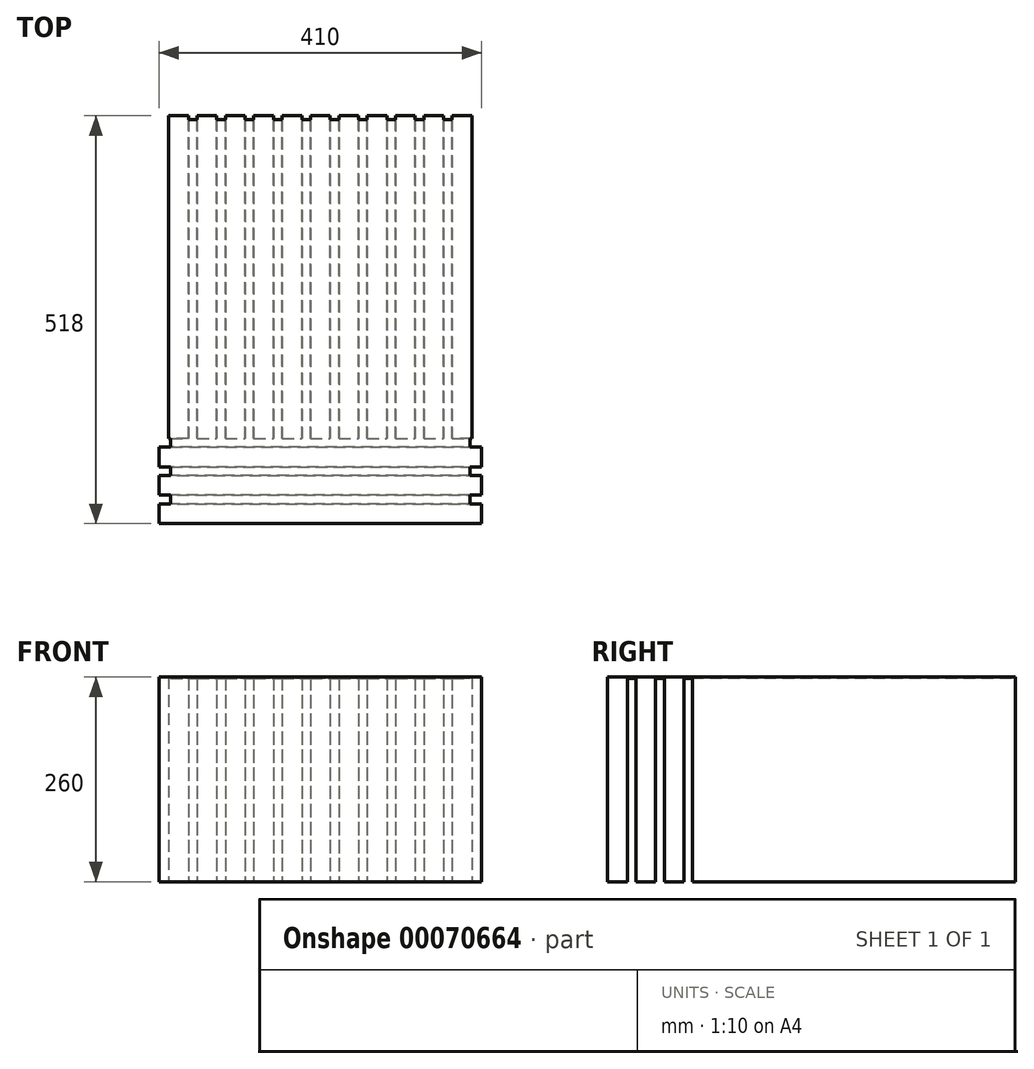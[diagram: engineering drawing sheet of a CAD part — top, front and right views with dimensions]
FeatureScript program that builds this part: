
annotation { "Feature Type Name" : "Feature", "Feature Type Description" : "" }
export const myFeature = defineFeature(function(context is Context, id is Id, definition is map)
    precondition{}
    {
        {
            var Q0;
            Q0=qCreatedBy(makeId("Top.planeOp"),FACE);
            cPlane(context, id + "F0", {"entities" : qUnion([Q0]), "cplaneType" : CPlaneType.OFFSET, "offset" : 258 * mm, "width" : 150 * mm, "height" : 150 * mm});
        }
        {
            var Q0;
            Q0=qCreatedBy(id+"F0.planeOp",FACE);
            var sketch = newSketch(context, id + "F1", { "sketchPlane" : qUnion([Q0])});
            skLineSegment(sketch, "E0.bottom", {"start": v(-190, 200) * mm, "end": v(190, 200) * mm});
            skLineSegment(sketch, "E0.top", {"start": v(-190, -300) * mm, "end": v(190, -300) * mm});
            skLineSegment(sketch, "E0.left", {"start": v(-190, 200) * mm, "end": v(-190, -300) * mm});
            skLineSegment(sketch, "E0.right", {"start": v(190, 200) * mm, "end": v(190, -300) * mm});
            skSolve(sketch);
        }
        {
            var Q0;
            Q0 = qSketchRegion(id + "F1", true);
            extrude(context, id + "F2", {"entities" : qUnion([Q0]), "depth" : 2 * mm});
        }
        {
            var Q0;
            Q0=qCreatedBy(makeId("Top.planeOp"),FACE);
            var sketch = newSketch(context, id + "F3", { "sketchPlane" : qUnion([Q0])});
            skLineSegment(sketch, "E1.rect.bottom", {"start": v(12.5, -205) * mm, "end": v(-12.5, -205) * mm});
            skLineSegment(sketch, "E1.rect.top", {"start": v(12.5, 205) * mm, "end": v(-12.5, 205) * mm});
            skLineSegment(sketch, "E1.rect.left", {"start": v(12.5, -205) * mm, "end": v(12.5, 205) * mm});
            skLineSegment(sketch, "E1.rect.right", {"start": v(-12.5, -205) * mm, "end": v(-12.5, 205) * mm});
            skPoint(sketch, "E1.rect.middle", {"position": v(0, 0) * mm});
            skLineSegment(sketch, "E2.1.0.0", {"start": v(48.5, -205) * mm, "end": v(23.5, -205) * mm});
            skLineSegment(sketch, "E2.1.0.1", {"start": v(48.5, -205) * mm, "end": v(48.5, 205) * mm});
            skLineSegment(sketch, "E2.1.0.2", {"start": v(23.5, -205) * mm, "end": v(23.5, 205) * mm});
            skPoint(sketch, "E2.1.0.3", {"position": v(36, 0) * mm});
            skLineSegment(sketch, "E2.1.0.4", {"start": v(48.5, 205) * mm, "end": v(23.5, 205) * mm});
            skLineSegment(sketch, "E2.2.0.0", {"start": v(84.5, -205) * mm, "end": v(59.5, -205) * mm});
            skLineSegment(sketch, "E2.2.0.1", {"start": v(84.5, -205) * mm, "end": v(84.5, 205) * mm});
            skLineSegment(sketch, "E2.2.0.2", {"start": v(59.5, -205) * mm, "end": v(59.5, 205) * mm});
            skPoint(sketch, "E2.2.0.3", {"position": v(72, 0) * mm});
            skLineSegment(sketch, "E2.2.0.4", {"start": v(84.5, 205) * mm, "end": v(59.5, 205) * mm});
            skLineSegment(sketch, "E2.direction1", {"start": v(-12.5, -205) * mm, "end": v(23.5, -205) * mm, "construction": true});
            skLineSegment(sketch, "E3.0.3.0", {"start": v(120.5, -205) * mm, "end": v(95.5, -205) * mm});
            skLineSegment(sketch, "E3.3.3.0", {"start": v(120.5, -205) * mm, "end": v(120.5, 205) * mm});
            skLineSegment(sketch, "E3.6.3.0", {"start": v(95.5, -205) * mm, "end": v(95.5, 205) * mm});
            skPoint(sketch, "E3.9.3.0", {"position": v(108, 0) * mm});
            skLineSegment(sketch, "E3.10.3.0", {"start": v(120.5, 205) * mm, "end": v(95.5, 205) * mm});
            skLineSegment(sketch, "E3.0.4.0", {"start": v(156.5, -205) * mm, "end": v(131.5, -205) * mm});
            skLineSegment(sketch, "E3.3.4.0", {"start": v(156.5, -205) * mm, "end": v(156.5, 205) * mm});
            skLineSegment(sketch, "E3.6.4.0", {"start": v(131.5, -205) * mm, "end": v(131.5, 205) * mm});
            skPoint(sketch, "E3.9.4.0", {"position": v(144, 0) * mm});
            skLineSegment(sketch, "E3.10.4.0", {"start": v(156.5, 205) * mm, "end": v(131.5, 205) * mm});
            skLineSegment(sketch, "E4.0.5.0", {"start": v(192.5, -205) * mm, "end": v(167.5, -205) * mm});
            skLineSegment(sketch, "E4.3.5.0", {"start": v(192.5, -205) * mm, "end": v(192.5, 205) * mm});
            skLineSegment(sketch, "E4.6.5.0", {"start": v(167.5, -205) * mm, "end": v(167.5, 205) * mm});
            skPoint(sketch, "E4.9.5.0", {"position": v(180, 0) * mm});
            skLineSegment(sketch, "E4.10.5.0", {"start": v(192.5, 205) * mm, "end": v(167.5, 205) * mm});
            skLineSegment(sketch, "E5.1.0.0", {"start": v(-23.5, -205) * mm, "end": v(-48.5, -205) * mm});
            skLineSegment(sketch, "E5.1.0.1", {"start": v(-23.5, -205) * mm, "end": v(-23.5, 205) * mm});
            skLineSegment(sketch, "E5.1.0.2", {"start": v(-48.5, -205) * mm, "end": v(-48.5, 205) * mm});
            skPoint(sketch, "E5.1.0.3", {"position": v(-36, 0) * mm});
            skLineSegment(sketch, "E5.1.0.4", {"start": v(-23.5, 205) * mm, "end": v(-48.5, 205) * mm});
            skLineSegment(sketch, "E5.2.0.0", {"start": v(-59.5, -205) * mm, "end": v(-84.5, -205) * mm});
            skLineSegment(sketch, "E5.2.0.1", {"start": v(-59.5, -205) * mm, "end": v(-59.5, 205) * mm});
            skLineSegment(sketch, "E5.2.0.2", {"start": v(-84.5, -205) * mm, "end": v(-84.5, 205) * mm});
            skPoint(sketch, "E5.2.0.3", {"position": v(-72, 0) * mm});
            skLineSegment(sketch, "E5.2.0.4", {"start": v(-59.5, 205) * mm, "end": v(-84.5, 205) * mm});
            skLineSegment(sketch, "E5.direction1", {"start": v(-12.5, -205) * mm, "end": v(-48.5, -205) * mm, "construction": true});
            skLineSegment(sketch, "E6.0.3.0", {"start": v(-95.5, -205) * mm, "end": v(-120.5, -205) * mm});
            skLineSegment(sketch, "E6.3.3.0", {"start": v(-95.5, -205) * mm, "end": v(-95.5, 205) * mm});
            skLineSegment(sketch, "E6.6.3.0", {"start": v(-120.5, -205) * mm, "end": v(-120.5, 205) * mm});
            skPoint(sketch, "E6.9.3.0", {"position": v(-108, 0) * mm});
            skLineSegment(sketch, "E6.10.3.0", {"start": v(-95.5, 205) * mm, "end": v(-120.5, 205) * mm});
            skLineSegment(sketch, "E6.0.4.0", {"start": v(-131.5, -205) * mm, "end": v(-156.5, -205) * mm});
            skLineSegment(sketch, "E6.3.4.0", {"start": v(-131.5, -205) * mm, "end": v(-131.5, 205) * mm});
            skLineSegment(sketch, "E6.6.4.0", {"start": v(-156.5, -205) * mm, "end": v(-156.5, 205) * mm});
            skPoint(sketch, "E6.9.4.0", {"position": v(-144, 0) * mm});
            skLineSegment(sketch, "E6.10.4.0", {"start": v(-131.5, 205) * mm, "end": v(-156.5, 205) * mm});
            skLineSegment(sketch, "E6.0.5.0", {"start": v(-167.5, -205) * mm, "end": v(-192.5, -205) * mm});
            skLineSegment(sketch, "E6.3.5.0", {"start": v(-167.5, -205) * mm, "end": v(-167.5, 205) * mm});
            skLineSegment(sketch, "E6.6.5.0", {"start": v(-192.5, -205) * mm, "end": v(-192.5, 205) * mm});
            skPoint(sketch, "E6.9.5.0", {"position": v(-180, 0) * mm});
            skLineSegment(sketch, "E6.10.5.0", {"start": v(-167.5, 205) * mm, "end": v(-192.5, 205) * mm});
            skLineSegment(sketch, "E7.rect.bottom", {"start": v(205, -216) * mm, "end": v(-205, -216) * mm});
            skLineSegment(sketch, "E7.rect.top", {"start": v(205, -241) * mm, "end": v(-205, -241) * mm});
            skLineSegment(sketch, "E7.rect.left", {"start": v(205, -216) * mm, "end": v(205, -241) * mm});
            skLineSegment(sketch, "E7.rect.right", {"start": v(-205, -216) * mm, "end": v(-205, -241) * mm});
            skPoint(sketch, "E7.rect.middle", {"position": v(0, -228.5) * mm});
            skLineSegment(sketch, "E8.rect.bottom", {"start": v(-205, -252) * mm, "end": v(205, -252) * mm});
            skLineSegment(sketch, "E8.rect.top", {"start": v(-205, -277) * mm, "end": v(205, -277) * mm});
            skLineSegment(sketch, "E8.rect.left", {"start": v(-205, -252) * mm, "end": v(-205, -277) * mm});
            skLineSegment(sketch, "E8.rect.right", {"start": v(205, -252) * mm, "end": v(205, -277) * mm});
            skPoint(sketch, "E8.rect.middle", {"position": v(0, -264.5) * mm});
            skLineSegment(sketch, "E9.rect.bottom", {"start": v(-205, -288) * mm, "end": v(205, -288) * mm});
            skLineSegment(sketch, "E9.rect.top", {"start": v(-205, -313) * mm, "end": v(205, -313) * mm});
            skLineSegment(sketch, "E9.rect.left", {"start": v(-205, -288) * mm, "end": v(-205, -313) * mm});
            skLineSegment(sketch, "E9.rect.right", {"start": v(205, -288) * mm, "end": v(205, -313) * mm});
            skPoint(sketch, "E9.rect.middle", {"position": v(0, -300.5) * mm});
            skSolve(sketch);
        }
        {
            var Q0;
            Q0 = qSketchRegion(id + "F3", true);
            extrude(context, id + "F4", {"entities" : qUnion([Q0]), "operationType" : NewBodyOperationType.ADD, "depth" : 260 * mm});
        }
    });
